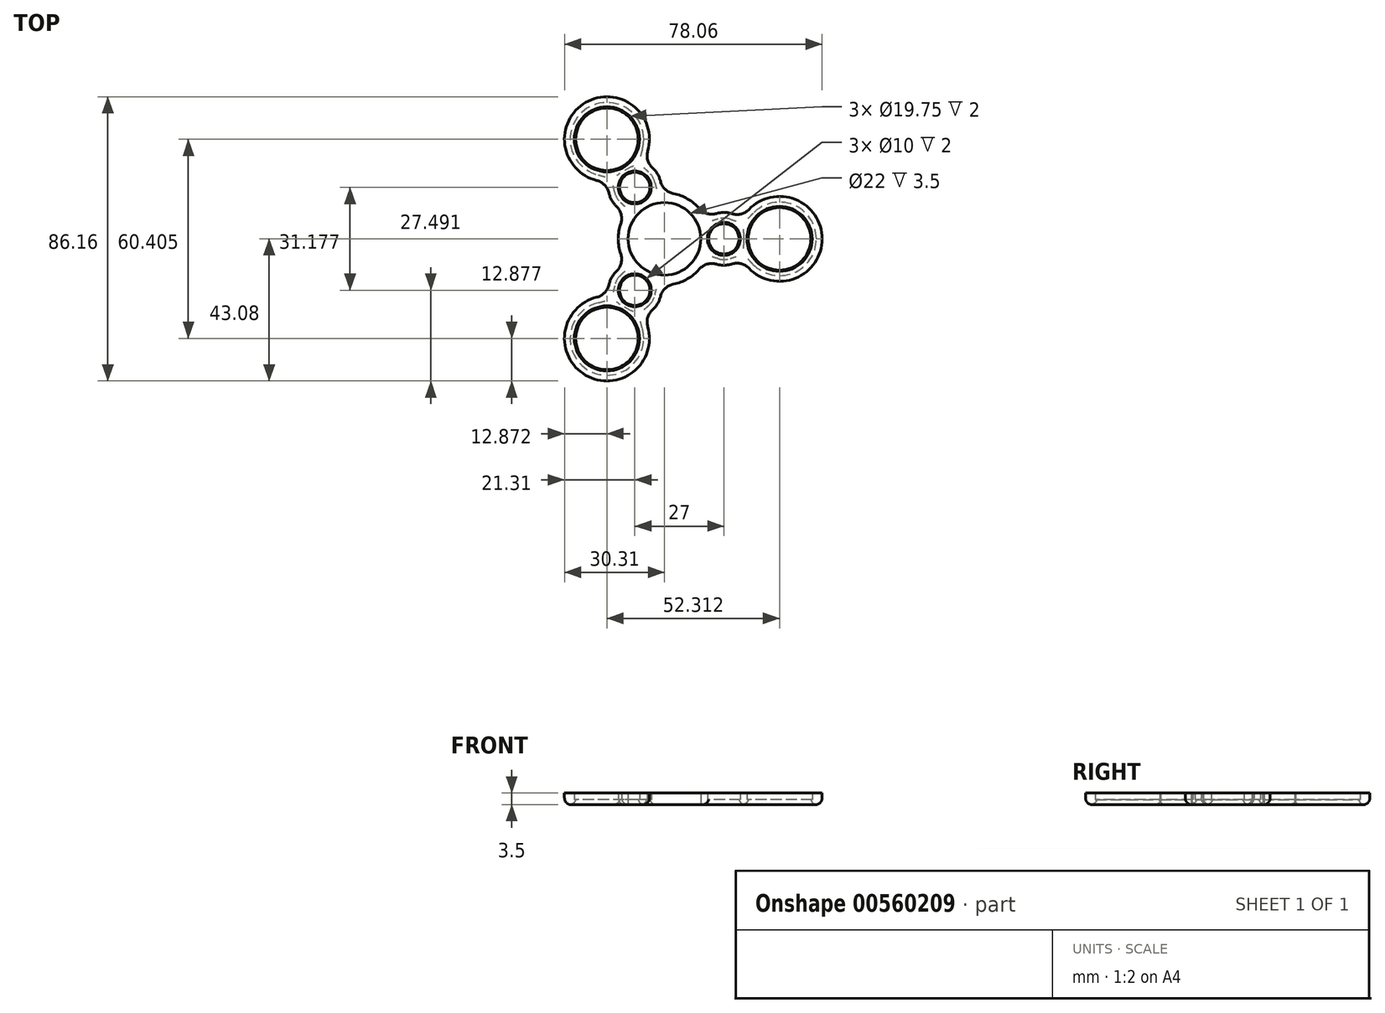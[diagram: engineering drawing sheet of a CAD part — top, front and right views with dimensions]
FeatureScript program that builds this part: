
annotation { "Feature Type Name" : "Feature", "Feature Type Description" : "" }
export const myFeature = defineFeature(function(context is Context, id is Id, definition is map)
    precondition{}
    {
        {
            var Q0;
            Q0=qCreatedBy(makeId("Top.planeOp"),FACE);
            var sketch = newSketch(context, id + "F0", { "sketchPlane" : qUnion([Q0])});
            skCircle(sketch, "E0", {"center": v(0, 0) * mm, "radius": 11 * mm});
            skCircle(sketch, "E1", {"center": v(18, 0) * mm, "radius": 5 * mm});
            skCircle(sketch, "E2", {"center": v(34.88, 0) * mm, "radius": 9.88 * mm});
            skArc(sketch, "E3.0", {"start": v(25.59, -8.91) * mm, "mid": v(47.75, 0) * mm, "end": v(25.59, 8.91) * mm});
            skArc(sketch, "E4.0", {"start": v(20.45, 7.62) * mm, "mid": v(18.1, 8) * mm, "end": v(15.74, 7.68) * mm});
            skArc(sketch, "E5.0", {"start": v(10.56, 9.2) * mm, "mid": v(7, 12.12) * mm, "end": v(2.68, 13.74) * mm});
            skArc(sketch, "E6.trimOffspring", {"start": v(15.74, -7.68) * mm, "mid": v(18.1, -8) * mm, "end": v(20.45, -7.62) * mm});
            skPoint(sketch, "E7.visualSharp", {"position": v(23.42, 5.88) * mm});
            skArc(sketch, "E7.filletArc", {"start": v(20.45, 7.62) * mm, "mid": v(23.2, 7.53) * mm, "end": v(25.59, 8.91) * mm});
            skPoint(sketch, "E8.visualSharp", {"position": v(12.67, 5.96) * mm});
            skArc(sketch, "E8.filletArc", {"start": v(10.56, 9.2) * mm, "mid": v(12.93, 7.67) * mm, "end": v(15.74, 7.68) * mm});
            skPoint(sketch, "E9.visualSharp", {"position": v(12.67, -5.96) * mm});
            skArc(sketch, "E9.filletArc", {"start": v(15.74, -7.68) * mm, "mid": v(12.93, -7.67) * mm, "end": v(10.56, -9.2) * mm});
            skPoint(sketch, "E10.visualSharp", {"position": v(23.42, -5.88) * mm});
            skArc(sketch, "E10.filletArc", {"start": v(25.59, -8.91) * mm, "mid": v(23.2, -7.53) * mm, "end": v(20.45, -7.62) * mm});
            skCircle(sketch, "E11", {"center": v(-9, 15.59) * mm, "radius": 5 * mm});
            skCircle(sketch, "E12", {"center": v(-9, -15.59) * mm, "radius": 5 * mm});
            skCircle(sketch, "E13", {"center": v(-17.44, 30.2) * mm, "radius": 9.88 * mm});
            skCircle(sketch, "E14", {"center": v(-17.44, -30.2) * mm, "radius": 9.88 * mm});
            skArc(sketch, "E15.0", {"start": v(-20.51, -17.7) * mm, "mid": v(-23.88, -41.35) * mm, "end": v(-5.07, -26.61) * mm});
            skArc(sketch, "E16.0", {"start": v(-14.52, -9.8) * mm, "mid": v(-15.98, -11.68) * mm, "end": v(-16.82, -13.9) * mm});
            skArc(sketch, "E17.0", {"start": v(-5.07, 26.61) * mm, "mid": v(-23.87, 41.35) * mm, "end": v(-20.51, 17.7) * mm});
            skArc(sketch, "E18.0", {"start": v(-16.82, 13.9) * mm, "mid": v(-15.98, 11.68) * mm, "end": v(-14.52, 9.8) * mm});
            skLineSegment(sketch, "E19.trimOffspring", {"start": v(-22.37, 38.75) * mm, "end": v(-23.87, 41.35) * mm});
            skArc(sketch, "E20.trimOffspring", {"start": v(-13.24, 4.55) * mm, "mid": v(-14, 0) * mm, "end": v(-13.24, -4.55) * mm});
            skArc(sketch, "E21.trimOffspring", {"start": v(-1.22, 17.47) * mm, "mid": v(-2.12, 19.67) * mm, "end": v(-3.63, 21.52) * mm});
            skArc(sketch, "E22.trimOffspring", {"start": v(2.68, -13.74) * mm, "mid": v(7, -12.12) * mm, "end": v(10.56, -9.2) * mm});
            skArc(sketch, "E23.trimOffspring", {"start": v(-3.63, -21.52) * mm, "mid": v(-2.12, -19.67) * mm, "end": v(-1.22, -17.47) * mm});
            skPoint(sketch, "E24.visualSharp", {"position": v(-6.62, 23.23) * mm});
            skArc(sketch, "E24.filletArc", {"start": v(-5.07, 26.61) * mm, "mid": v(-5.08, 23.86) * mm, "end": v(-3.63, 21.52) * mm});
            skPoint(sketch, "E25.visualSharp", {"position": v(-16.8, 17.34) * mm});
            skArc(sketch, "E25.filletArc", {"start": v(-16.82, 13.9) * mm, "mid": v(-18.12, 16.33) * mm, "end": v(-20.51, 17.7) * mm});
            skPoint(sketch, "E26.visualSharp", {"position": v(-11.5, 7.99) * mm});
            skArc(sketch, "E26.filletArc", {"start": v(-13.24, 4.55) * mm, "mid": v(-13.11, 7.36) * mm, "end": v(-14.52, 9.8) * mm});
            skPoint(sketch, "E27.visualSharp", {"position": v(-1.17, 13.95) * mm});
            skArc(sketch, "E27.filletArc", {"start": v(-1.22, 17.47) * mm, "mid": v(0.18, 15.03) * mm, "end": v(2.68, 13.74) * mm});
            skPoint(sketch, "E28.visualSharp", {"position": v(-11.5, -7.99) * mm});
            skArc(sketch, "E28.filletArc", {"start": v(-14.52, -9.8) * mm, "mid": v(-13.11, -7.36) * mm, "end": v(-13.24, -4.55) * mm});
            skPoint(sketch, "E29.visualSharp", {"position": v(-16.8, -17.34) * mm});
            skArc(sketch, "E29.filletArc", {"start": v(-20.51, -17.7) * mm, "mid": v(-18.12, -16.33) * mm, "end": v(-16.82, -13.9) * mm});
            skPoint(sketch, "E30.visualSharp", {"position": v(-6.62, -23.23) * mm});
            skArc(sketch, "E30.filletArc", {"start": v(-3.63, -21.52) * mm, "mid": v(-5.08, -23.86) * mm, "end": v(-5.07, -26.61) * mm});
            skPoint(sketch, "E31.visualSharp", {"position": v(-1.17, -13.95) * mm});
            skArc(sketch, "E31.filletArc", {"start": v(2.68, -13.74) * mm, "mid": v(0.18, -15.03) * mm, "end": v(-1.22, -17.47) * mm});
            skCircle(sketch, "E32.0", {"center": v(-17.44, 30.2) * mm, "radius": 9.48 * mm});
            skCircle(sketch, "E33.0", {"center": v(-9, 15.59) * mm, "radius": 4.6 * mm});
            skCircle(sketch, "E34.0", {"center": v(18, 0) * mm, "radius": 4.6 * mm});
            skCircle(sketch, "E35.0", {"center": v(34.88, 0) * mm, "radius": 9.48 * mm});
            skCircle(sketch, "E36.0", {"center": v(-9, -15.59) * mm, "radius": 4.6 * mm});
            skCircle(sketch, "E37.0", {"center": v(-17.44, -30.2) * mm, "radius": 9.48 * mm});
            skSolve(sketch);
        }
        {
            var Q0;
            Q0=makeQuery(id+"F0.imprint","IMPRINT",FACE,{"disambiguationData":[TD([[makeQuery(id+"F0.imprint","IMPRINT",EDGE,{"derivedFrom":sQuery(id+"F0.wireOp",EDGE,"E0")}),-1.0]])]});
            extrude(context, id + "F1", {"entities" : qUnion([Q0]), "depth" : 3.5 * mm, "offsetDistance" : 25 * mm});
        }
        {
            var Q0;
            Q0=makeQuery(id+"F0.imprint","IMPRINT",FACE,{"disambiguationData":[TD([[makeQuery(id+"F0.imprint","IMPRINT",EDGE,{"derivedFrom":sQuery(id+"F0.wireOp",EDGE,"E13")}),1.0]])]});
            var Q1;
            Q1=makeQuery(id+"F0.imprint","IMPRINT",FACE,{"disambiguationData":[TD([[makeQuery(id+"F0.imprint","IMPRINT",EDGE,{"derivedFrom":sQuery(id+"F0.wireOp",EDGE,"E11")}),1.0]])]});
            var Q2;
            Q2=makeQuery(id+"F0.imprint","IMPRINT",FACE,{"disambiguationData":[TD([[makeQuery(id+"F0.imprint","IMPRINT",EDGE,{"derivedFrom":sQuery(id+"F0.wireOp",EDGE,"E12")}),1.0]])]});
            var Q3;
            Q3=makeQuery(id+"F0.imprint","IMPRINT",FACE,{"disambiguationData":[TD([[makeQuery(id+"F0.imprint","IMPRINT",EDGE,{"derivedFrom":sQuery(id+"F0.wireOp",EDGE,"E14")}),1.0]])]});
            var Q4;
            Q4=makeQuery(id+"F0.imprint","IMPRINT",FACE,{"disambiguationData":[TD([[makeQuery(id+"F0.imprint","IMPRINT",EDGE,{"derivedFrom":sQuery(id+"F0.wireOp",EDGE,"E2")}),1.0]])]});
            var Q5;
            Q5=makeQuery(id+"F0.imprint","IMPRINT",FACE,{"disambiguationData":[TD([[makeQuery(id+"F0.imprint","IMPRINT",EDGE,{"derivedFrom":sQuery(id+"F0.wireOp",EDGE,"E1")}),1.0]])]});
            extrude(context, id + "F2", {"entities" : qUnion([Q0, Q1, Q2, Q3, Q4, Q5]), "operationType" : NewBodyOperationType.ADD, "depth" : 1.5 * mm, "offsetDistance" : 25 * mm});
        }
        {
            var Q0;
            Q0=makeQuery(id+"F1.opExtrude","CAP_EDGE",EDGE,{"disambiguationData":[OSD([sQuery(id+"F0.wireOp",EDGE,"E15.0")])],"isStart":true});
            fillet(context, id + "F3", {"entities" : qUnion([Q0]), "radius" : 2 * mm, "tangentPropagation" : true, "allowEdgeOverflow" : false});
        }
        {
            var Q0;
            Q0=makeQuery(id+"F2.opExtrude","CAP_EDGE",EDGE,{"disambiguationData":[OSD([sQuery(id+"F0.wireOp",EDGE,"E33.0")])],"isStart":true});
            var Q1;
            Q1=makeQuery(id+"F2.opExtrude","CAP_EDGE",EDGE,{"disambiguationData":[OSD([sQuery(id+"F0.wireOp",EDGE,"E36.0")])],"isStart":true});
            var Q2;
            Q2=makeQuery(id+"F2.opExtrude","CAP_EDGE",EDGE,{"disambiguationData":[OSD([sQuery(id+"F0.wireOp",EDGE,"E32.0")])],"isStart":true});
            var Q3;
            Q3=makeQuery(id+"F2.opExtrude","CAP_EDGE",EDGE,{"disambiguationData":[OSD([sQuery(id+"F0.wireOp",EDGE,"E37.0")])],"isStart":true});
            var Q4;
            Q4=makeQuery(id+"F2.opExtrude","CAP_EDGE",EDGE,{"disambiguationData":[OSD([sQuery(id+"F0.wireOp",EDGE,"E34.0")])],"isStart":true});
            var Q5;
            Q5=makeQuery(id+"F2.opExtrude","CAP_EDGE",EDGE,{"disambiguationData":[OSD([sQuery(id+"F0.wireOp",EDGE,"E35.0")])],"isStart":true});
            fillet(context, id + "F4", {"entities" : qUnion([Q0, Q1, Q2, Q3, Q4, Q5]), "radius" : 2 * mm, "tangentPropagation" : true, "allowEdgeOverflow" : false});
        }
    });
